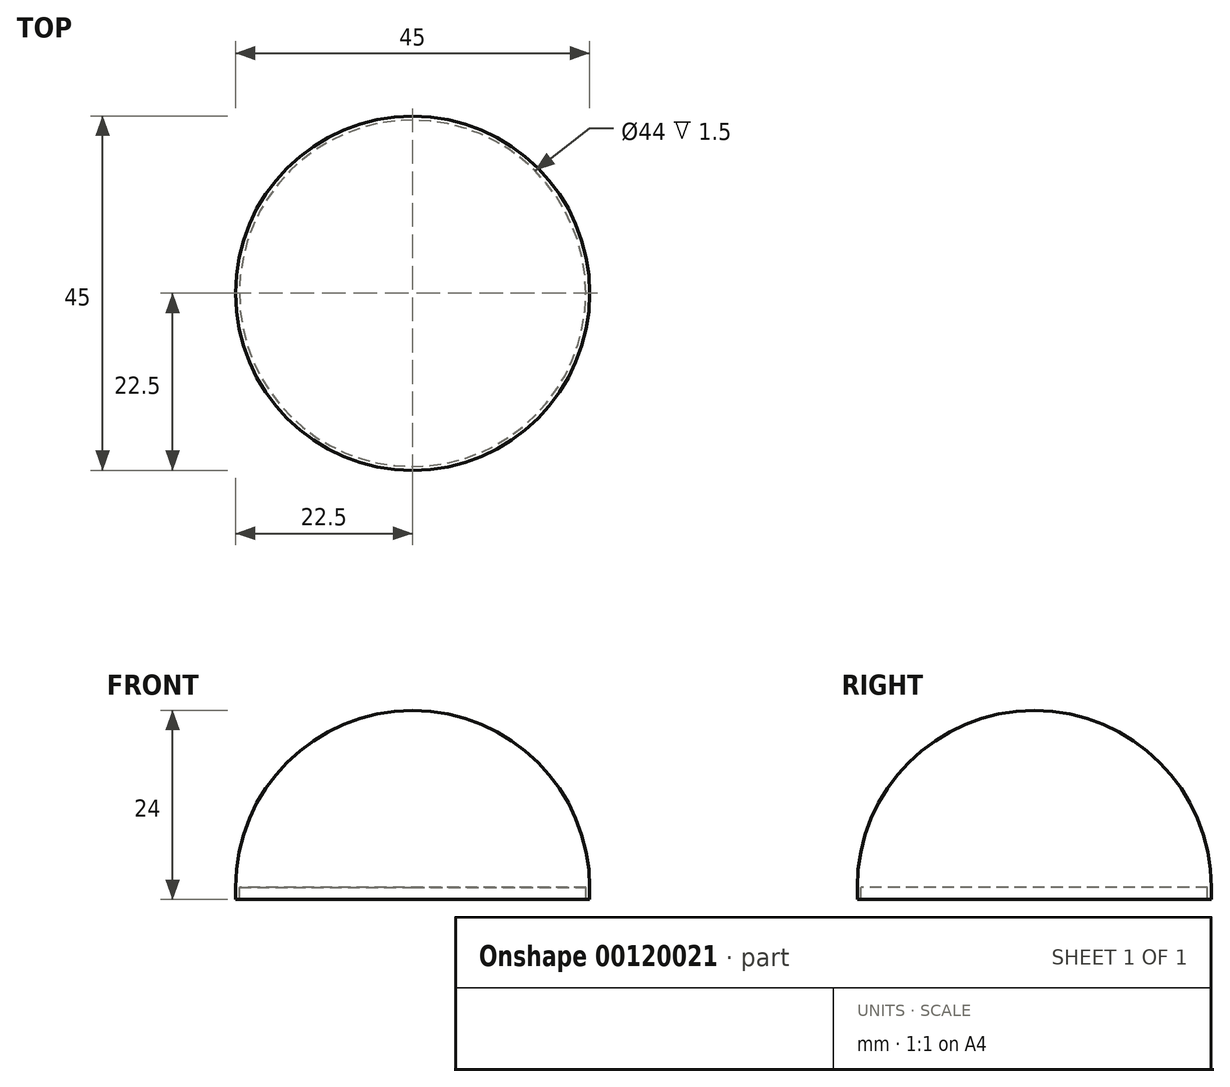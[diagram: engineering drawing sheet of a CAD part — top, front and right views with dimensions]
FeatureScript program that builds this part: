
annotation { "Feature Type Name" : "Feature", "Feature Type Description" : "" }
export const myFeature = defineFeature(function(context is Context, id is Id, definition is map)
    precondition{}
    {
        {
            var Q0;
            Q0=qCreatedBy(makeId("Top.planeOp"),FACE);
            var sketch = newSketch(context, id + "F0", { "sketchPlane" : qUnion([Q0])});
            skCircle(sketch, "E0", {"center": v(0, 0) * mm, "radius": 22.5 * mm});
            skLineSegment(sketch, "E1", {"start": v(-22.5, 0) * mm, "end": v(22.5, 0) * mm});
            skSolve(sketch);
        }
        {
            var Q0;
            {var subQ0=sQuery(id+"F0.wireOp",EDGE,"E1");Q0=makeQuery(id+"F0.imprint","IMPRINT",FACE,{"disambiguationData":[TD([[makeQuery(id+"F0.imprint","IMPRINT",EDGE,{"derivedFrom":subQ0}),1.0]])]});}
            var Q1;
            Q1=sQuery(id+"F0.wireOp",EDGE,"E1");
            revolve(context, id + "F1", {"entities" : qUnion([Q0]), "axis" : qUnion([Q1]), "revolveType" : RevolveType.ONE_DIRECTION, "angle" : 180 * degree});
        }
        {
            var Q0;
            Q0=makeQuery(id+"F1.opRevolve","CAP_FACE",FACE,{"disambiguationData":[OSD([sQuery(id+"F0.wireOp",EDGE,"E0"),sQuery(id+"F0.wireOp",EDGE,"E1")])],"isStart":true});
            var sketch = newSketch(context, id + "F2", { "sketchPlane" : qUnion([Q0])});
            skCircle(sketch, "E2.0", {"center": v(0, 0) * mm, "radius": 22 * mm});
            skCircle(sketch, "E3.0", {"center": v(0, 0) * mm, "radius": 22.5 * mm});
            skSolve(sketch);
        }
        {
            var Q0;
            Q0=makeQuery(id+"F2.imprint","IMPRINT",FACE,{"disambiguationData":[TD([[makeQuery(id+"F2.imprint","IMPRINT",EDGE,{"derivedFrom":sQuery(id+"F2.wireOp",EDGE,"E2.0")}),-1.0]])]});
            extrude(context, id + "F3", {"entities" : qUnion([Q0]), "operationType" : NewBodyOperationType.ADD, "depth" : 1.5 * mm});
        }
    });
